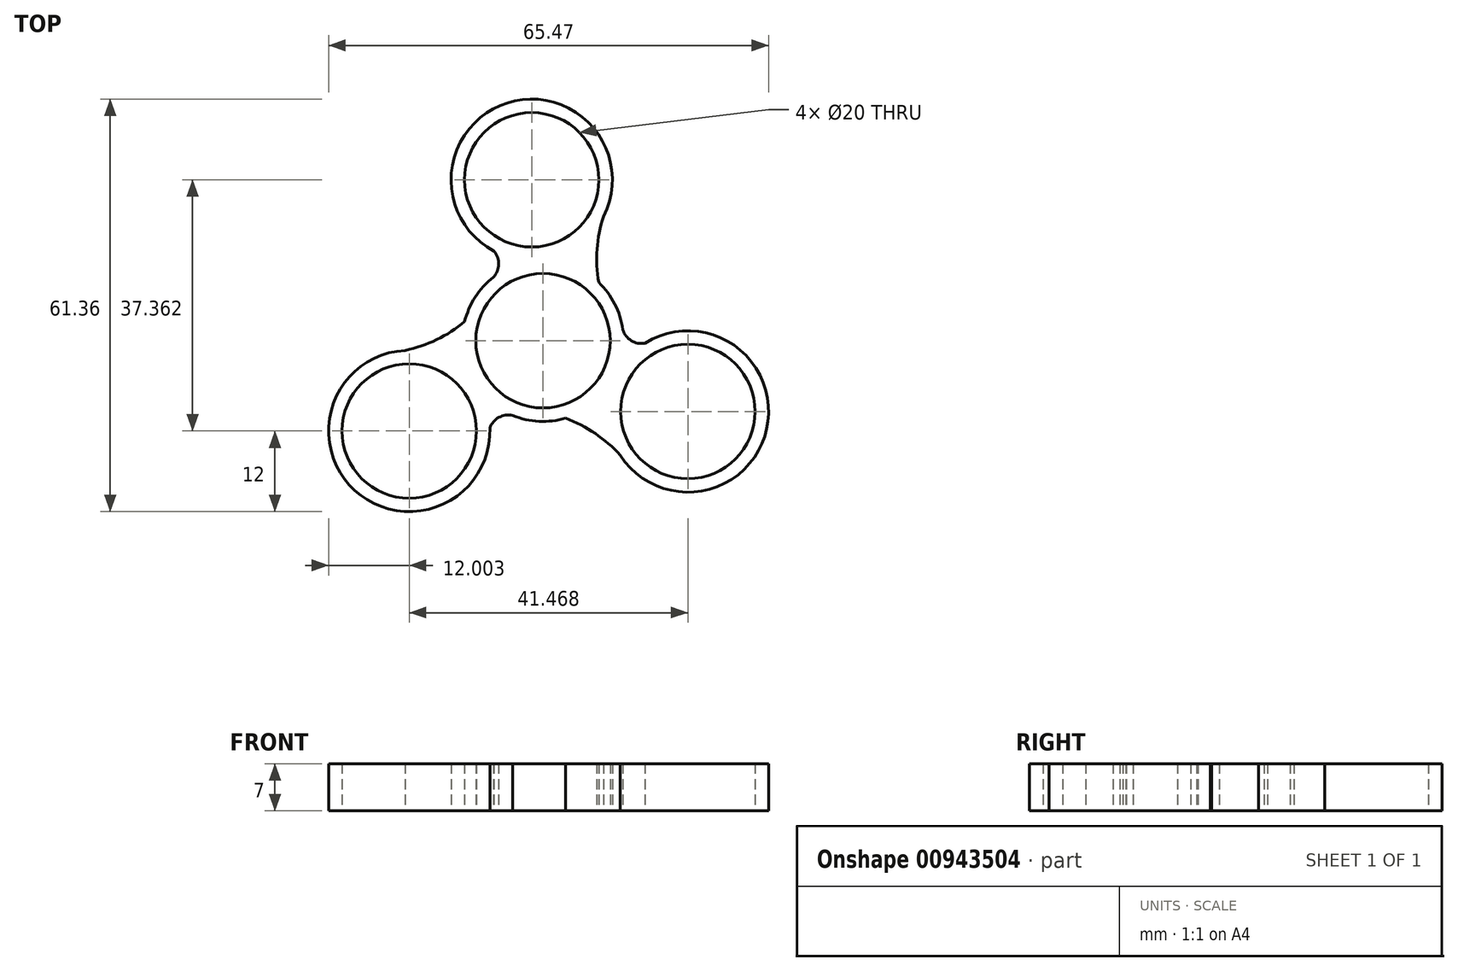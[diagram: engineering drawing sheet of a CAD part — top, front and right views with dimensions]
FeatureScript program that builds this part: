
annotation { "Feature Type Name" : "Feature", "Feature Type Description" : "" }
export const myFeature = defineFeature(function(context is Context, id is Id, definition is map)
    precondition{}
    {
        {
            var Q0;
            Q0=qCreatedBy(makeId("Top.planeOp"),FACE);
            var sketch = newSketch(context, id + "F0", { "sketchPlane" : qUnion([Q0])});
            skCircle(sketch, "E0", {"center": v(0, 0) * mm, "radius": 10 * mm});
            skCircle(sketch, "E1.0", {"center": v(0, 0) * mm, "radius": 12 * mm});
            skCircle(sketch, "E2", {"center": v(-19.9, -13.42) * mm, "radius": 10 * mm});
            skCircle(sketch, "E3.0", {"center": v(-19.9, -13.42) * mm, "radius": 12 * mm});
            skArc(sketch, "E4", {"start": v(-3.85, -11.36) * mm, "mid": v(-7, -11.7) * mm, "end": v(-7.97, -14.73) * mm});
            skArc(sketch, "E5", {"start": v(-20.51, -1.44) * mm, "mid": v(-15.83, 0.16) * mm, "end": v(-11.66, 2.83) * mm});
            skArc(sketch, "E6.1.0", {"start": v(11.5, -17.05) * mm, "mid": v(7.78, -13.79) * mm, "end": v(3.38, -11.51) * mm});
            skCircle(sketch, "E6.1.1", {"center": v(21.57, -10.52) * mm, "radius": 12 * mm});
            skCircle(sketch, "E6.1.2", {"center": v(21.57, -10.52) * mm, "radius": 10 * mm});
            skArc(sketch, "E6.1.3", {"start": v(11.77, 2.35) * mm, "mid": v(13.64, -0.22) * mm, "end": v(16.74, 0.46) * mm});
            skArc(sketch, "E6.2.0", {"start": v(9.01, 18.48) * mm, "mid": v(8.05, 13.63) * mm, "end": v(8.28, 8.68) * mm});
            skCircle(sketch, "E6.2.1", {"center": v(-1.67, 23.94) * mm, "radius": 12 * mm});
            skCircle(sketch, "E6.2.2", {"center": v(-1.67, 23.94) * mm, "radius": 10 * mm});
            skArc(sketch, "E6.2.3", {"start": v(-7.92, 9.02) * mm, "mid": v(-6.63, 11.92) * mm, "end": v(-8.77, 14.26) * mm});
            skSolve(sketch);
        }
        {
            var Q0;
            Q0=makeQuery(id+"F0.imprint","IMPRINT",FACE,{"disambiguationData":[TD([[makeQuery(id+"F0.imprint","IMPRINT",EDGE,{"derivedFrom":sQuery(id+"F0.wireOp",EDGE,"E2")}),-1.0]])]});
            var Q1;
            Q1=makeQuery(id+"F0.imprint","IMPRINT",FACE,{"disambiguationData":[TD([[makeQuery(id+"F0.imprint","IMPRINT",EDGE,{"derivedFrom":sQuery(id+"F0.wireOp",EDGE,"E0")}),-1.0]])]});
            var Q2;
            {var subQ0=sQuery(id+"F0.wireOp",EDGE,"E5");Q2=makeQuery(id+"F0.imprint","IMPRINT",FACE,{"disambiguationData":[TD([[makeQuery(id+"F0.imprint","IMPRINT",EDGE,{"derivedFrom":subQ0}),-1.0]])]});}
            var Q3;
            {var subQ0=sQuery(id+"F0.wireOp",EDGE,"E4");var subQ1=sQuery(id+"F0.wireOp",EDGE,"E1.0");var subQ2=makeQuery(id+"F0.imprint","INTERSECT",VERTEX,{"disambiguationData":[OD(1.0)],"derivedFrom":[subQ1,subQ0]});Q3=makeQuery(id+"F0.imprint","IMPRINT",FACE,{"disambiguationData":[TD([[makeQuery(id+"F0.imprint","IMPRINT",EDGE,{"disambiguationData":[TD([[subQ2,1.0]])],"derivedFrom":subQ1}),-1.0]])]});}
            extrude(context, id + "F1", {"entities" : qUnion([Q0, Q1, Q2, Q3]), "depth" : 7 * mm, "offsetDistance" : 25 * mm});
        }
        {
            var Q0;
            Q0 = qSketchRegion(id + "F0", true);
            extrude(context, id + "F2", {"entities" : qUnion([Q0]), "operationType" : NewBodyOperationType.ADD, "depth" : 7 * mm, "offsetDistance" : 25 * mm});
        }
    });
